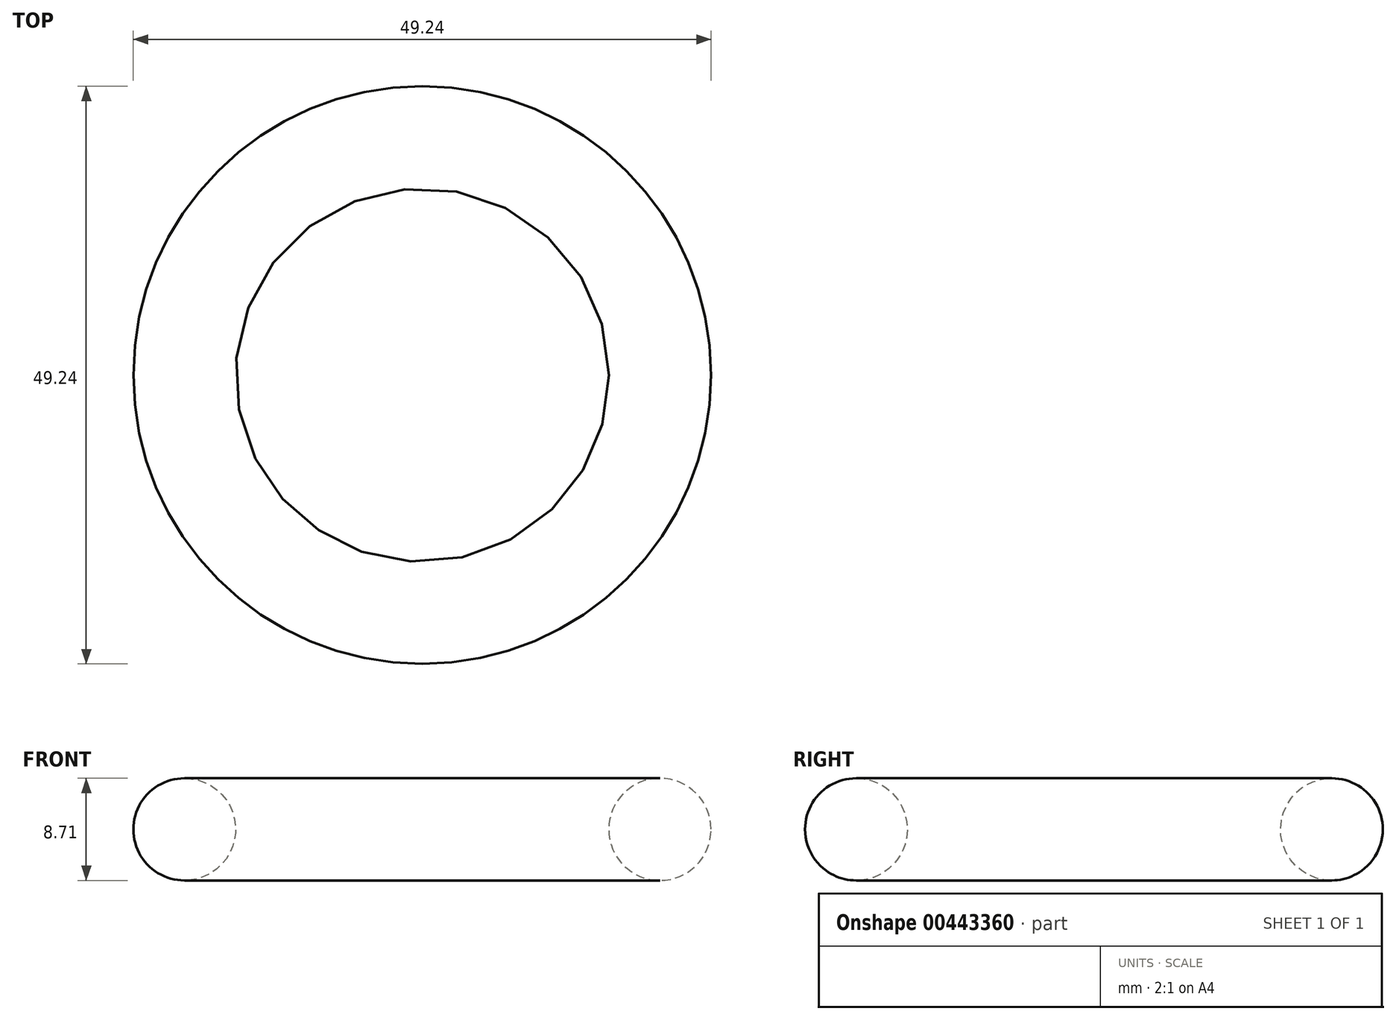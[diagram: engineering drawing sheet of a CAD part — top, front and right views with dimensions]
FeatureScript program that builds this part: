
annotation { "Feature Type Name" : "Feature", "Feature Type Description" : "" }
export const myFeature = defineFeature(function(context is Context, id is Id, definition is map)
    precondition{}
    {
        {
            var Q0;
            Q0=qCreatedBy(makeId("Front.planeOp"),FACE);
            var sketch = newSketch(context, id + "F0", { "sketchPlane" : qUnion([Q0])});
            skLineSegment(sketch, "E0", {"start": v(0, 77.29) * mm, "end": v(0, -75.53) * mm});
            skSolve(sketch);
        }
        {
            var Q0;
            Q0=qCreatedBy(makeId("Front.planeOp"),FACE);
            var sketch = newSketch(context, id + "F1", { "sketchPlane" : qUnion([Q0])});
            skCircle(sketch, "E1", {"center": v(20.26, 4.62) * mm, "radius": 4.36 * mm});
            skSolve(sketch);
        }
        {
            var Q0;
            Q0=qCreatedBy(makeId("Front.planeOp"),FACE);
            var sketch = newSketch(context, id + "F2", { "sketchPlane" : qUnion([Q0])});
            skLineSegment(sketch, "E2", {"start": v(0, 77.12) * mm, "end": v(0, -76.6) * mm});
            skSolve(sketch);
        }
        {
            var Q0;
            Q0=makeQuery(id+"F1.imprint","IMPRINT",FACE,{"disambiguationData":[TD([[makeQuery(id+"F1.imprint","IMPRINT",EDGE,{"derivedFrom":sQuery(id+"F1.wireOp",EDGE,"E1")}),1.0]])]});
            var Q1;
            Q1=sQuery(id+"F2.wireOp",EDGE,"E2");
            revolve(context, id + "F3", {"entities" : qUnion([Q0]), "axis" : qUnion([Q1]), "revolveType" : RevolveType.FULL});
        }
        {
            var Q0;
            Q0=qCreatedBy(makeId("Front.planeOp"),FACE);
            var sketch = newSketch(context, id + "F4", { "sketchPlane" : qUnion([Q0])});
            skLineSegment(sketch, "E3", {"start": v(0, 69.9) * mm, "end": v(19.9, 9) * mm});
            skLineSegment(sketch, "E4", {"start": v(19.9, 9) * mm, "end": v(0, 9) * mm});
            skSolve(sketch);
        }
        {
            var Q0;
            Q0=sQuery(id+"F4.wireOp",EDGE,"E3");
            var Q1;
            Q1=sQuery(id+"F4.wireOp",EDGE,"E4");
            var Q2;
            Q2=sQuery(id+"F0.wireOp",EDGE,"E0");
            revolve(context, id + "F5", {"bodyType" : ToolBodyType.SURFACE, "surfaceEntities" : qUnion([Q0, Q1]), "axis" : qUnion([Q2]), "revolveType" : RevolveType.FULL});
        }
        {
            var Q0;
            Q0=qCreatedBy(makeId("Front.planeOp"),FACE);
            var sketch = newSketch(context, id + "F6", { "sketchPlane" : qUnion([Q0])});
            skArc(sketch, "E5", {"start": v(0, 75.53) * mm, "mid": v(-5, 70.6) * mm, "end": v(0, 65.68) * mm});
            skSolve(sketch);
        }
        {
            var Q0;
            Q0=sQuery(id+"F6.wireOp",EDGE,"E5");
            var Q1;
            Q1=sQuery(id+"F0.wireOp",EDGE,"E0");
            revolve(context, id + "F7", {"bodyType" : ToolBodyType.SURFACE, "surfaceEntities" : qUnion([Q0]), "axis" : qUnion([Q1]), "revolveType" : RevolveType.FULL});
        }
    });
